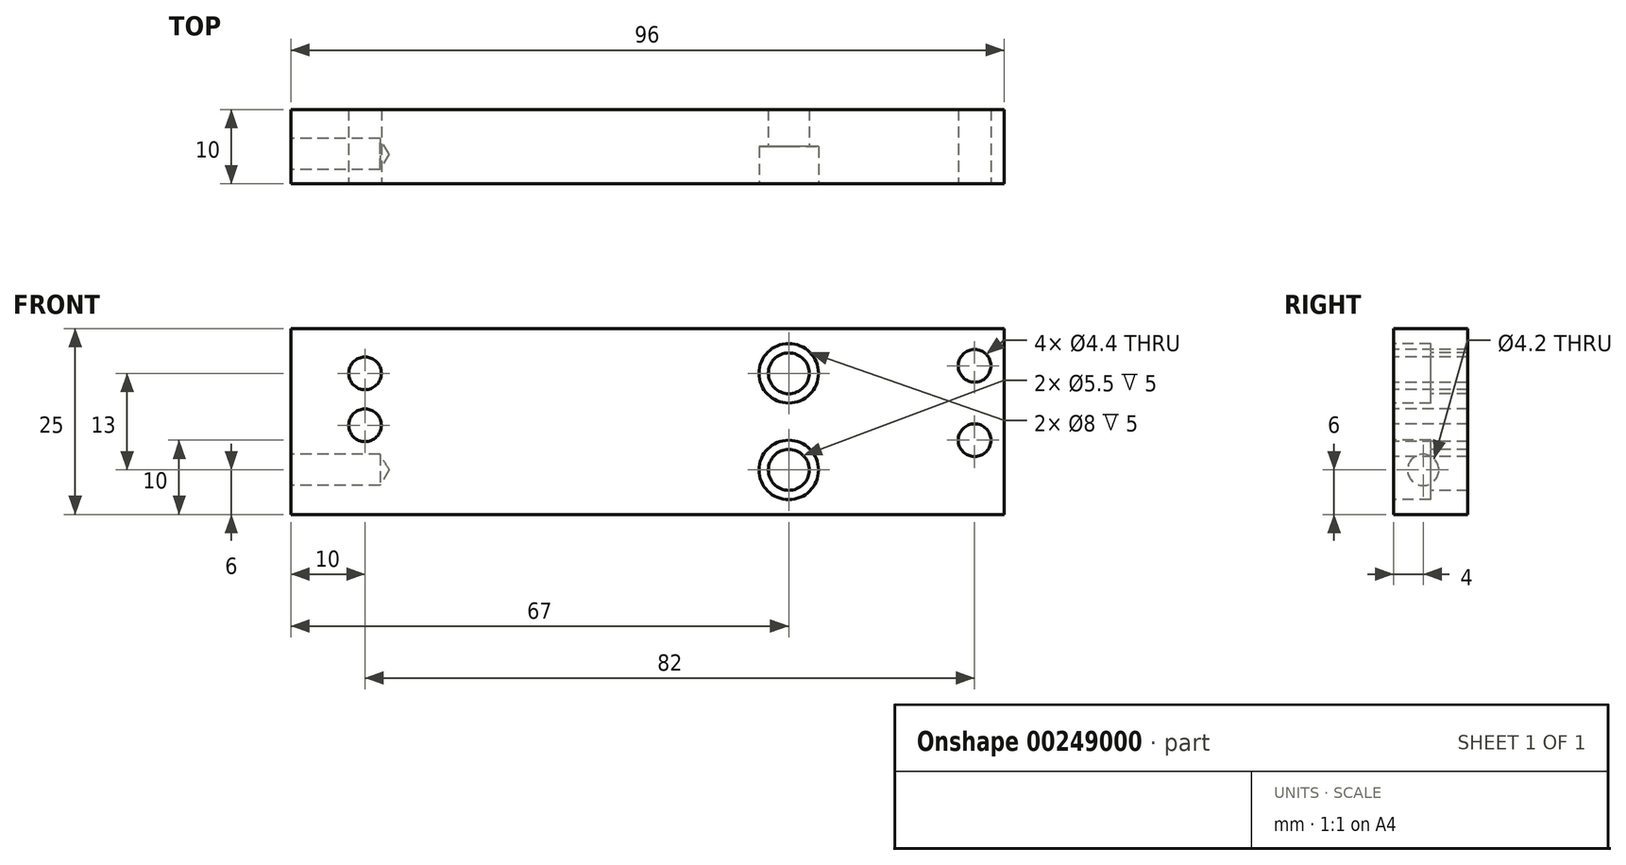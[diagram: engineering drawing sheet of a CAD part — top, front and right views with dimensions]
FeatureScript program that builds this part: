
annotation { "Feature Type Name" : "Feature", "Feature Type Description" : "" }
export const myFeature = defineFeature(function(context is Context, id is Id, definition is map)
    precondition{}
    {
        {
            var Q0;
            Q0=qCreatedBy(makeId("Front.planeOp"),FACE);
            var sketch = newSketch(context, id + "F0", { "sketchPlane" : qUnion([Q0])});
            skLineSegment(sketch, "E0.bottom", {"start": v(48, 12.5) * mm, "end": v(-48, 12.5) * mm});
            skLineSegment(sketch, "E0.top", {"start": v(48, -12.5) * mm, "end": v(-48, -12.5) * mm});
            skLineSegment(sketch, "E0.left", {"start": v(48, 12.5) * mm, "end": v(48, -12.5) * mm});
            skLineSegment(sketch, "E0.right", {"start": v(-48, 12.5) * mm, "end": v(-48, -12.5) * mm});
            skPoint(sketch, "E0.middle", {"position": v(0, 0) * mm});
            skPoint(sketch, "E1", {"position": v(44, 7.5) * mm});
            skPoint(sketch, "E2", {"position": v(44, -2.5) * mm});
            skPoint(sketch, "E3", {"position": v(19, -6.5) * mm});
            skPoint(sketch, "E4", {"position": v(19, 6.5) * mm});
            skPoint(sketch, "E5", {"position": v(-38, 6.5) * mm});
            skPoint(sketch, "E6", {"position": v(-38, -0.5) * mm});
            skSolve(sketch);
        }
        {
            var Q0;
            Q0=makeQuery(id+"F0.imprint","IMPRINT",FACE,{"disambiguationData":[TD([[makeQuery(id+"F0.imprint","IMPRINT",EDGE,{"derivedFrom":sQuery(id+"F0.wireOp",EDGE,"E0.bottom")}),1.0]])]});
            extrude(context, id + "F1", {"entities" : qUnion([Q0]), "oppositeDirection" : true, "depth" : 10 * mm});
        }
        {
            var Q0;
            Q0=sQuery(id+"F0.wireOp",VERTEX,"E4");
            var Q1;
            Q1=sQuery(id+"F0.wireOp",VERTEX,"E3");
            var Q2;
            Q2=makeQuery(id+"F1.opExtrude","SWEPT_BODY",BODY,{"disambiguationData":[OSD([sQuery(id+"F0.wireOp",EDGE,"E0.bottom"),sQuery(id+"F0.wireOp",EDGE,"E0.top"),sQuery(id+"F0.wireOp",EDGE,"E0.left"),sQuery(id+"F0.wireOp",EDGE,"E0.right")])]});
            hole(context, id + "F2", {"style" : HoleStyle.C_BORE, "endStyle" : HoleEndStyle.THROUGH, "holeDiameter" : 5.5 * mm, "cBoreDiameter" : 8 * mm, "cBoreDepth" : 5 * mm, "tappedDepth" : 12 * mm, "tapClearance" : 3, "startFromSketch" : true, "locations" : qUnion([Q0, Q1]), "scope" : qUnion([Q2])});
        }
        {
            var Q0;
            Q0=sQuery(id+"F0.wireOp",VERTEX,"E1");
            var Q1;
            Q1=sQuery(id+"F0.wireOp",VERTEX,"E2");
            var Q2;
            Q2=sQuery(id+"F0.wireOp",VERTEX,"E5");
            var Q3;
            Q3=sQuery(id+"F0.wireOp",VERTEX,"E6");
            var Q4;
            Q4=makeQuery(id+"F1.opExtrude","SWEPT_BODY",BODY,{"disambiguationData":[OSD([sQuery(id+"F0.wireOp",EDGE,"E0.bottom"),sQuery(id+"F0.wireOp",EDGE,"E0.top"),sQuery(id+"F0.wireOp",EDGE,"E0.left"),sQuery(id+"F0.wireOp",EDGE,"E0.right")])]});
            hole(context, id + "F3", {"style" : HoleStyle.SIMPLE, "endStyle" : HoleEndStyle.THROUGH, "standardTappedOrClearance" : lookupTablePath({ "standard" : "ISO", "fit" : "Normal", "size" : "M4", "type" : "Clearance" }), "standardBlindInLast" : lookupTablePath({ "fit" : "Standard", "standard" : "ISO", "size" : "M4", "type" : "Clearance" }), "holeDiameter" : 4.4 * mm, "tappedDepth" : 12 * mm, "tapClearance" : 3, "startFromSketch" : true, "locations" : qUnion([Q0, Q1, Q2, Q3]), "scope" : qUnion([Q4])});
        }
        {
            var Q0;
            Q0=makeQuery(id+"F1.opExtrude","SWEPT_FACE",FACE,{"disambiguationData":[OSD([sQuery(id+"F0.wireOp",EDGE,"E0.right")])]});
            var sketch = newSketch(context, id + "F4", { "sketchPlane" : qUnion([Q0])});
            skPoint(sketch, "E7", {"position": v(-4, -6.5) * mm});
            skSolve(sketch);
        }
        {
            var Q0;
            Q0=sQuery(id+"F4.wireOp",VERTEX,"E7");
            var Q1;
            Q1=makeQuery(id+"F1.opExtrude","SWEPT_BODY",BODY,{"disambiguationData":[OSD([sQuery(id+"F0.wireOp",EDGE,"E0.bottom"),sQuery(id+"F0.wireOp",EDGE,"E0.top"),sQuery(id+"F0.wireOp",EDGE,"E0.left"),sQuery(id+"F0.wireOp",EDGE,"E0.right")])]});
            hole(context, id + "F5", {"style" : HoleStyle.SIMPLE, "endStyle" : HoleEndStyle.BLIND, "standardTappedOrClearance" : lookupTablePath({ "standard" : "ISO", "engagement" : "75%", "pitch" : "0.8 mm", "size" : "M5", "type" : "Tapped" }), "standardBlindInLast" : lookupTablePath({ "standard" : "ISO", "engagement" : "75%", "pitch" : "0.8 mm", "size" : "M5", "type" : "Tapped" }), "holeDiameter" : 4.2 * mm, "showTappedDepth" : true, "holeDepth" : 12 * mm, "tappedDepth" : 9.6 * mm, "tapClearance" : 3, "startFromSketch" : true, "locations" : qUnion([Q0]), "scope" : qUnion([Q1]), "majorDiameter" : 5 * mm});
        }
    });
